# Revit family: Electronics_Communication_Talkaphone_AOR-Analog-Station_Flush-Mounted
name_source: partatom
category: Telephone Devices
units: mm (PartAtom-declared; Revit-internal decimal feet)

## family parameters
Cut with Voids When Loaded = No
Host = Face
Maintain Annotation Orientation = No
OmniClass Number = 23.37.27.17
OmniClass Title = Emergency Call Equipment
Part Type = Normal
Room Calculation Point = No
Round Connector Dimension = Use Diameter
Shared = No

## types (1)
- Area of Rescue Analog Station, Flush Mounted
    Assembly Code = D5030300
    Communication = Half-duplex two-way hands-free communication
    Connection = Tip and ring flying leads for field installation
    Construction = #4 brushed 304 stainless steel faceplate, 0.09 in. (2.2mm)
    Default Elevation = 48 "
    Depth = 2.75 "
    Description = THIS FLUSH MOUNT AOR ANALOG CALL STATION IS AN INDOOR, HANDS-FREE ADA-COMPLIANT COMMUNICATION ENDPOINT FOR USE WITH AN ANALOG AOR COMMAND UNIT IN AN AREA OF RESCUE ASSISTANCE.
    Digital Capacity = Up to 20-digits, including 4-second pause, for each of five (5) phone numbers
    Edition number = 1
    Environment = For indoor use
    Height = 8.23 "
    Keynote = 27 30 00
    Manufacturer = Talkaphone
    Model = AOR-CSE-FM
    Mounting = Flush mount
    Operating Temperature = 32ºF to +158ºF (0ºC to +70ºC)
    Power Source = Line-powered by Analog Command Unit (requires 20mA at 24 V off-hook)
    Product Guid = f8b6c517-c9ec-4259-9b88-6e6cfc2d865f
    Product Material = Talkaphone - Stainless Steel
    Product data url = https://www.bimobject.com
    Programming = Programming of the Analog Stations can be carried out via touch-tone commands sent through the phone built into the Analog Command Unit. All programming is stored on non-volatile EEPROM.
    Relative Humidity = Up to 95% non-condensing
    URL = https://www.talkaphone.com
    Warranty = 5-year limited warranty
    Width = 4.75 "
    Wiring = One (1) twisted, shielded pair per station not to exceed 25 ohms resistance
    “On Time” = Programmable for no limit or from 1 to 9 minutes in 1-minute increments

## geometry (parser evidence)
native form markers: Sweep x3
no freeform markers — native parametric forms only
